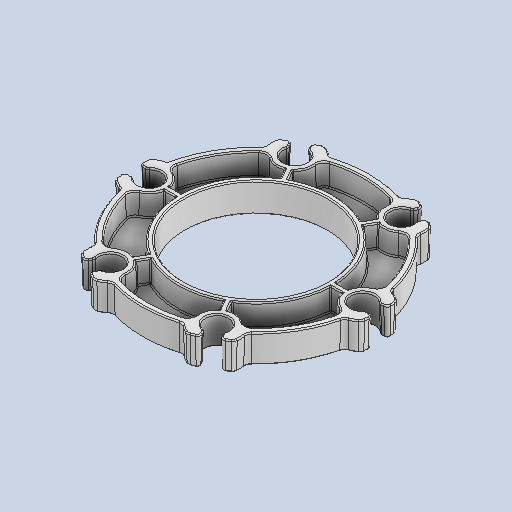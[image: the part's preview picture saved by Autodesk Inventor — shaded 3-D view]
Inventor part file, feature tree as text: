
AUTODESK INVENTOR PART (.ipt)
format: ipt  version: 2023 (Build 270158000, 158)  size: 988,672 bytes
history: native  units: in
note: dims shown in document units (in); Inventor stores cm internally (conversion verified against a paired STEP export)
features: fillet x1
ambient origin geometry x8: Origin, YZ Plane, XZ Plane, XY Plane, X Axis, Y Axis, Z Axis, Center Point
bodies: Solid1 (feature_tree)
feature tree (1):
  fillet  "Fillet3"  [1 undecoded]
note: 1 required parameter value undecoded (feature->parameter linkage not recoverable at this tier; creation-order binding heuristic only, values carry confidence <= 0.55)
